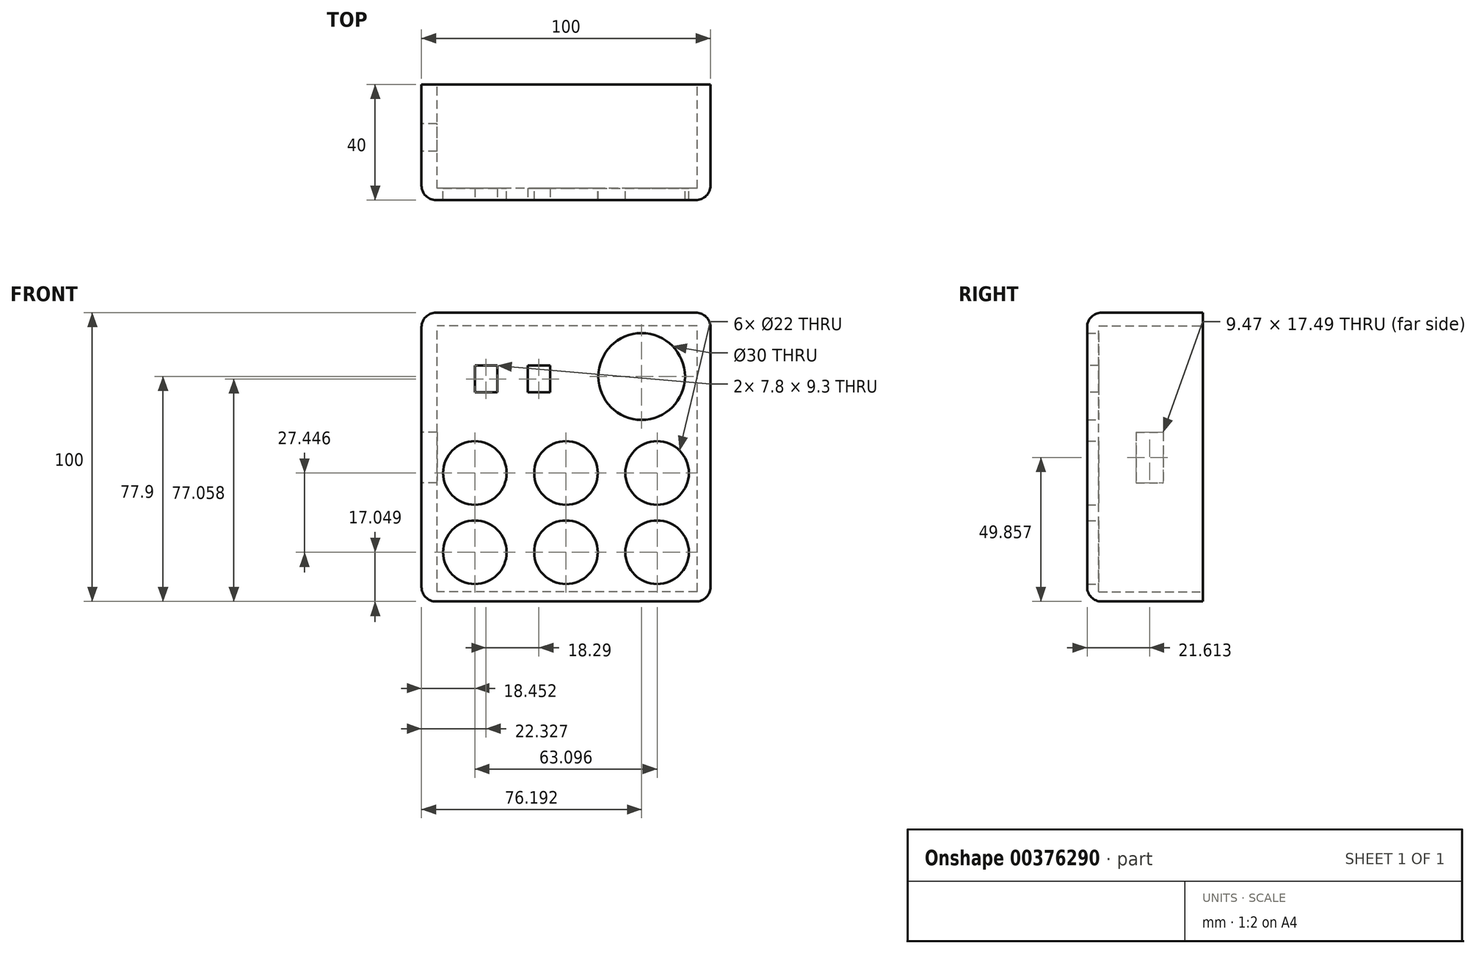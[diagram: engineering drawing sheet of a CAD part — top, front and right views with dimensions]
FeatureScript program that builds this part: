
annotation { "Feature Type Name" : "Feature", "Feature Type Description" : "" }
export const myFeature = defineFeature(function(context is Context, id is Id, definition is map)
    precondition{}
    {
        {
            var Q0;
            Q0=qCreatedBy(makeId("Front.planeOp"),FACE);
            var sketch = newSketch(context, id + "F0", { "sketchPlane" : qUnion([Q0])});
            skLineSegment(sketch, "E0.bottom", {"start": v(-50, 50) * mm, "end": v(50, 50) * mm});
            skLineSegment(sketch, "E0.top", {"start": v(-50, -50) * mm, "end": v(50, -50) * mm});
            skLineSegment(sketch, "E0.left", {"start": v(-50, 50) * mm, "end": v(-50, -50) * mm});
            skLineSegment(sketch, "E0.right", {"start": v(50, 50) * mm, "end": v(50, -50) * mm});
            skPoint(sketch, "E0.middle", {"position": v(0, 0) * mm});
            skCircle(sketch, "E1", {"center": v(0, -32.95) * mm, "radius": 11 * mm});
            skCircle(sketch, "E2", {"center": v(-31.55, -32.95) * mm, "radius": 11 * mm});
            skCircle(sketch, "E3.MirrorC", {"center": v(31.55, -32.95) * mm, "radius": 11 * mm});
            skCircle(sketch, "E4", {"center": v(26.2, 27.9) * mm, "radius": 15 * mm});
            skCircle(sketch, "E5", {"center": v(0, -5.5) * mm, "radius": 11 * mm});
            skCircle(sketch, "E6", {"center": v(-31.55, -5.5) * mm, "radius": 11 * mm});
            skCircle(sketch, "E7.MirrorC", {"center": v(31.55, -5.5) * mm, "radius": 11 * mm});
            skSolve(sketch);
        }
        {
            var Q0;
            Q0 = qSketchRegion(id + "F0", true);
            extrude(context, id + "F1", {"entities" : qUnion([Q0]), "depth" : 40 * mm});
        }
        {
            var Q0;
            Q0=makeQuery(id+"F1.opExtrude","CAP_FACE",FACE,{"disambiguationData":[OSD([sQuery(id+"F0.wireOp",EDGE,"E0.bottom"),sQuery(id+"F0.wireOp",EDGE,"E0.top"),sQuery(id+"F0.wireOp",EDGE,"E0.left"),sQuery(id+"F0.wireOp",EDGE,"E0.right"),sQuery(id+"F0.wireOp",EDGE,"E1"),sQuery(id+"F0.wireOp",EDGE,"E2"),sQuery(id+"F0.wireOp",EDGE,"E3.MirrorC"),sQuery(id+"F0.wireOp",EDGE,"E4"),sQuery(id+"F0.wireOp",EDGE,"E5"),sQuery(id+"F0.wireOp",EDGE,"E6"),sQuery(id+"F0.wireOp",EDGE,"E7.MirrorC")])],"isStart":true});
            var sketch = newSketch(context, id + "F2", { "sketchPlane" : qUnion([Q0])});
            skLineSegment(sketch, "E8.bottom", {"start": v(-45.4, -46.62) * mm, "end": v(44.6, -46.62) * mm});
            skLineSegment(sketch, "E8.top", {"start": v(-45.4, 45.38) * mm, "end": v(44.6, 45.38) * mm});
            skLineSegment(sketch, "E8.left", {"start": v(-45.4, -46.62) * mm, "end": v(-45.4, 45.38) * mm});
            skLineSegment(sketch, "E8.right", {"start": v(44.6, -46.62) * mm, "end": v(44.6, 45.38) * mm});
            skSolve(sketch);
        }
        {
            var Q0;
            Q0 = qSketchRegion(id + "F2", true);
            extrude(context, id + "F3", {"entities" : qUnion([Q0]), "operationType" : NewBodyOperationType.REMOVE, "oppositeDirection" : true, "depth" : 36 * mm});
        }
        {
            var Q0;
            Q0=makeQuery(id+"F1.opExtrude","CAP_FACE",FACE,{"disambiguationData":[OSD([sQuery(id+"F0.wireOp",EDGE,"E0.bottom"),sQuery(id+"F0.wireOp",EDGE,"E0.top"),sQuery(id+"F0.wireOp",EDGE,"E0.left"),sQuery(id+"F0.wireOp",EDGE,"E0.right"),sQuery(id+"F0.wireOp",EDGE,"E1"),sQuery(id+"F0.wireOp",EDGE,"E2"),sQuery(id+"F0.wireOp",EDGE,"E3.MirrorC"),sQuery(id+"F0.wireOp",EDGE,"E4"),sQuery(id+"F0.wireOp",EDGE,"E5"),sQuery(id+"F0.wireOp",EDGE,"E6"),sQuery(id+"F0.wireOp",EDGE,"E7.MirrorC")])],"isStart":false});
            var sketch = newSketch(context, id + "F4", { "sketchPlane" : qUnion([Q0])});
            skLineSegment(sketch, "E9.bottom", {"start": v(-5.48, 22.4) * mm, "end": v(-13.28, 22.4) * mm});
            skLineSegment(sketch, "E9.top", {"start": v(-5.48, 31.7) * mm, "end": v(-13.28, 31.7) * mm});
            skLineSegment(sketch, "E9.left", {"start": v(-5.48, 22.4) * mm, "end": v(-5.48, 31.7) * mm});
            skLineSegment(sketch, "E9.right", {"start": v(-13.28, 22.4) * mm, "end": v(-13.28, 31.7) * mm});
            skLineSegment(sketch, "E10.bottom", {"start": v(-23.77, 22.4) * mm, "end": v(-31.57, 22.4) * mm});
            skLineSegment(sketch, "E10.top", {"start": v(-23.77, 31.7) * mm, "end": v(-31.57, 31.7) * mm});
            skLineSegment(sketch, "E10.left", {"start": v(-23.77, 22.4) * mm, "end": v(-23.77, 31.7) * mm});
            skLineSegment(sketch, "E10.right", {"start": v(-31.57, 22.4) * mm, "end": v(-31.57, 31.7) * mm});
            skSolve(sketch);
        }
        {
            var Q0;
            Q0 = qSketchRegion(id + "F4", true);
            extrude(context, id + "F5", {"entities" : qUnion([Q0]), "operationType" : NewBodyOperationType.REMOVE, "oppositeDirection" : true, "depth" : 25 * mm});
        }
        {
            var Q0;
            Q0=makeQuery(id+"F1.opExtrude","CAP_EDGE",EDGE,{"disambiguationData":[OSD([sQuery(id+"F0.wireOp",EDGE,"E0.right")])],"isStart":false});
            fillet(context, id + "F6", {"entities" : qUnion([Q0]), "radius" : 5 * mm, "tangentPropagation" : true, "allowEdgeOverflow" : false});
        }
        {
            var Q0;
            Q0=makeQuery(id+"F1.opExtrude","CAP_EDGE",EDGE,{"disambiguationData":[OSD([sQuery(id+"F0.wireOp",EDGE,"E0.left")])],"isStart":false});
            fillet(context, id + "F7", {"entities" : qUnion([Q0]), "radius" : 5 * mm, "tangentPropagation" : true, "allowEdgeOverflow" : false});
        }
        {
            var Q0;
            Q0=makeQuery(id+"F1.opExtrude","CAP_EDGE",EDGE,{"disambiguationData":[OSD([sQuery(id+"F0.wireOp",EDGE,"E0.top")])],"isStart":false});
            var Q1;
            Q1=makeQuery(id+"F1.opExtrude","CAP_EDGE",EDGE,{"disambiguationData":[OSD([sQuery(id+"F0.wireOp",EDGE,"E0.bottom")])],"isStart":false});
            fillet(context, id + "F8", {"entities" : qUnion([Q0, Q1]), "radius" : 5 * mm, "tangentPropagation" : true, "allowEdgeOverflow" : false});
        }
        {
            var Q0;
            Q0=makeQuery(id+"F1.opExtrude","SWEPT_FACE",FACE,{"disambiguationData":[OSD([sQuery(id+"F0.wireOp",EDGE,"E0.left")])]});
            var sketch = newSketch(context, id + "F9", { "sketchPlane" : qUnion([Q0])});
            skLineSegment(sketch, "E11.bottom", {"start": v(23.12, 8.6) * mm, "end": v(13.65, 8.6) * mm});
            skLineSegment(sketch, "E11.top", {"start": v(23.12, -8.89) * mm, "end": v(13.65, -8.89) * mm});
            skLineSegment(sketch, "E11.left", {"start": v(23.12, 8.6) * mm, "end": v(23.12, -8.89) * mm});
            skLineSegment(sketch, "E11.right", {"start": v(13.65, 8.6) * mm, "end": v(13.65, -8.89) * mm});
            skSolve(sketch);
        }
        {
            var Q0;
            Q0 = qSketchRegion(id + "F9", true);
            extrude(context, id + "F10", {"entities" : qUnion([Q0]), "operationType" : NewBodyOperationType.REMOVE, "oppositeDirection" : true, "depth" : 25 * mm});
        }
    });
